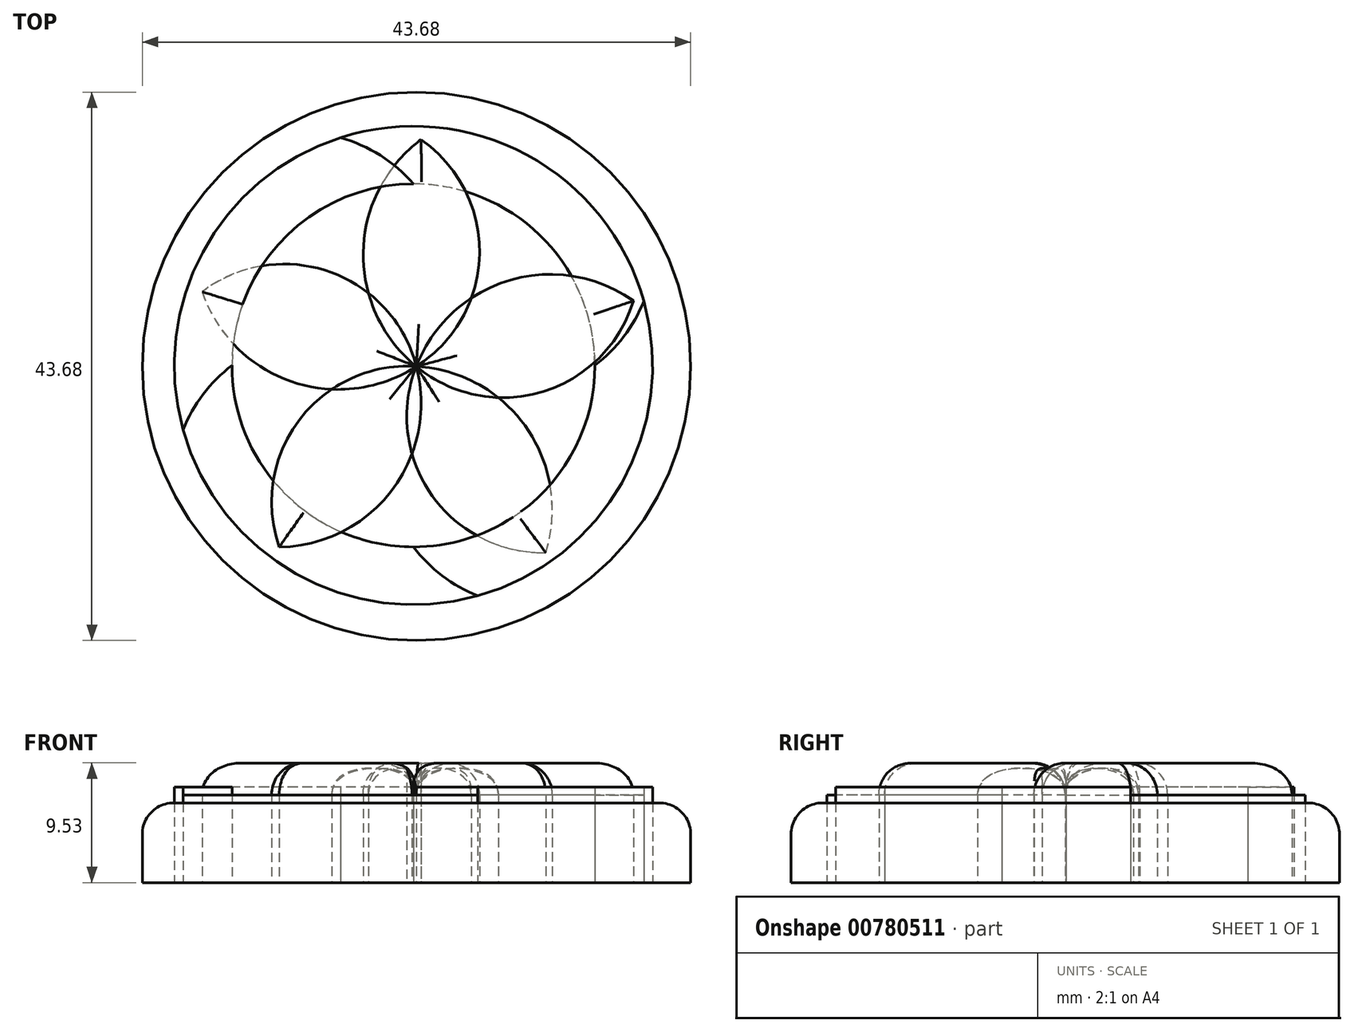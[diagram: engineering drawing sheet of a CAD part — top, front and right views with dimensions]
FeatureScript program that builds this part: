
annotation { "Feature Type Name" : "Feature", "Feature Type Description" : "" }
export const myFeature = defineFeature(function(context is Context, id is Id, definition is map)
    precondition{}
    {
        {
            var Q0;
            Q0=qCreatedBy(makeId("Top.planeOp"),FACE);
            var sketch = newSketch(context, id + "F0", { "sketchPlane" : qUnion([Q0])});
            skCircle(sketch, "E0", {"center": v(0, 0) * mm, "radius": 28.91 * mm});
            skCircle(sketch, "E1", {"center": v(0, 0) * mm, "radius": 38.1 * mm});
            skArc(sketch, "E2", {"start": v(0, 28.91) * mm, "mid": v(-32.59, 32.3) * mm, "end": v(-38.1, 0) * mm});
            skArc(sketch, "E3", {"start": v(-28.91, 0) * mm, "mid": v(-33.5, -33.5) * mm, "end": v(0, -38.1) * mm});
            skArc(sketch, "E4", {"start": v(0, -28.91) * mm, "mid": v(33.5, -33.5) * mm, "end": v(38.1, 0) * mm});
            skArc(sketch, "E5", {"start": v(28.91, 0) * mm, "mid": v(33.5, 33.5) * mm, "end": v(0, 38.1) * mm});
            skArc(sketch, "E6", {"start": v(-14.46, -19.05) * mm, "mid": v(-2.57, -13.06) * mm, "end": v(0, 0) * mm});
            skArc(sketch, "E7", {"start": v(0, 0) * mm, "mid": v(-12.34, -5.65) * mm, "end": v(-14.46, -19.05) * mm});
            skArc(sketch, "E8.1.0", {"start": v(13.76, -20.22) * mm, "mid": v(11.73, -7.06) * mm, "end": v(0.1, -0.58) * mm});
            skArc(sketch, "E8.1.1", {"start": v(0.1, -0.58) * mm, "mid": v(1.66, -14.06) * mm, "end": v(13.76, -20.22) * mm});
            skArc(sketch, "E8.2.0", {"start": v(23.59, 6.25) * mm, "mid": v(10.45, 8.4) * mm, "end": v(0.7, -0.66) * mm});
            skArc(sketch, "E8.2.1", {"start": v(0.7, -0.66) * mm, "mid": v(14, -3.35) * mm, "end": v(23.59, 6.25) * mm});
            skArc(sketch, "E8.3.0", {"start": v(1.45, 23.78) * mm, "mid": v(-4.64, 11.95) * mm, "end": v(0.95, -0.13) * mm});
            skArc(sketch, "E8.3.1", {"start": v(0.95, -0.13) * mm, "mid": v(7.61, 11.7) * mm, "end": v(1.45, 23.78) * mm});
            skArc(sketch, "E8.4.0", {"start": v(-22.06, 8.14) * mm, "mid": v(-12.7, -1.3) * mm, "end": v(0.52, 0.28) * mm});
            skArc(sketch, "E8.4.1", {"start": v(0.52, 0.28) * mm, "mid": v(-8.66, 10.27) * mm, "end": v(-22.06, 8.14) * mm});
            skPoint(sketch, "E8.center", {"position": v(0.45, -0.22) * mm});
            skSolve(sketch);
        }
        {
            var Q0;
            Q0=qCreatedBy(makeId("Top.planeOp"),FACE);
            var sketch = newSketch(context, id + "F1", { "sketchPlane" : qUnion([Q0])});
            skArc(sketch, "E9", {"start": v(-21.38, -28.93) * mm, "mid": v(-3.43, -19.88) * mm, "end": v(0.46, -0.15) * mm});
            skArc(sketch, "E10", {"start": v(0.46, -0.15) * mm, "mid": v(-18.19, -8.68) * mm, "end": v(-21.38, -28.93) * mm});
            skArc(sketch, "E11.1.0", {"start": v(21.08, -29.82) * mm, "mid": v(18.02, -9.94) * mm, "end": v(0.46, -0.15) * mm});
            skArc(sketch, "E11.1.1", {"start": v(0.46, -0.15) * mm, "mid": v(2.8, -20.52) * mm, "end": v(21.08, -29.82) * mm});
            skArc(sketch, "E11.2.0", {"start": v(35.04, 10.3) * mm, "mid": v(15.2, 13.52) * mm, "end": v(0.46, -0.15) * mm});
            skArc(sketch, "E11.2.1", {"start": v(0.46, -0.15) * mm, "mid": v(20.56, -4.21) * mm, "end": v(35.04, 10.3) * mm});
            skArc(sketch, "E11.3.0", {"start": v(1.2, 35.97) * mm, "mid": v(-8, 18.1) * mm, "end": v(0.46, -0.15) * mm});
            skArc(sketch, "E11.3.1", {"start": v(0.46, -0.15) * mm, "mid": v(10.53, 17.7) * mm, "end": v(1.2, 35.97) * mm});
            skArc(sketch, "E11.4.0", {"start": v(-33.66, 11.72) * mm, "mid": v(-19.5, -2.55) * mm, "end": v(0.46, -0.15) * mm});
            skArc(sketch, "E11.4.1", {"start": v(0.46, -0.15) * mm, "mid": v(-13.42, 14.94) * mm, "end": v(-33.66, 11.72) * mm});
            skSolve(sketch);
        }
        {
            var Q0;
            {var subQ1=sQuery(id+"F1.wireOp",EDGE,"E11.3.1");var subQ2=sQuery(id+"F1.wireOp",EDGE,"E11.3.0");var subQ6=makeQuery(id+"F1.imprint","INTERSECT",VERTEX,{"derivedFrom":[subQ2,subQ1]});Q0=makeQuery(id+"F1.imprint","IMPRINT",FACE,{"disambiguationData":[TD([[makeQuery(id+"F1.imprint","IMPRINT",EDGE,{"disambiguationData":[TD([[subQ6,-1.0]])],"derivedFrom":subQ2}),1.0]])]});}
            var Q1;
            {var subQ1=sQuery(id+"F1.wireOp",EDGE,"E11.2.1");var subQ2=sQuery(id+"F1.wireOp",EDGE,"E11.2.0");var subQ6=makeQuery(id+"F1.imprint","INTERSECT",VERTEX,{"derivedFrom":[subQ2,subQ1]});Q1=makeQuery(id+"F1.imprint","IMPRINT",FACE,{"disambiguationData":[TD([[makeQuery(id+"F1.imprint","IMPRINT",EDGE,{"disambiguationData":[TD([[subQ6,-1.0]])],"derivedFrom":subQ2}),1.0]])]});}
            var Q2;
            {var subQ1=sQuery(id+"F1.wireOp",EDGE,"E11.1.1");var subQ2=sQuery(id+"F1.wireOp",EDGE,"E11.1.0");var subQ6=makeQuery(id+"F1.imprint","INTERSECT",VERTEX,{"derivedFrom":[subQ2,subQ1]});Q2=makeQuery(id+"F1.imprint","IMPRINT",FACE,{"disambiguationData":[TD([[makeQuery(id+"F1.imprint","IMPRINT",EDGE,{"disambiguationData":[TD([[subQ6,-1.0]])],"derivedFrom":subQ2}),1.0]])]});}
            var Q3;
            {var subQ0=sQuery(id+"F1.wireOp",EDGE,"E11.4.1");var subQ1=sQuery(id+"F1.wireOp",EDGE,"E11.4.0");var subQ7=makeQuery(id+"F1.imprint","INTERSECT",VERTEX,{"derivedFrom":[subQ1,subQ0]});Q3=makeQuery(id+"F1.imprint","IMPRINT",FACE,{"disambiguationData":[TD([[makeQuery(id+"F1.imprint","IMPRINT",EDGE,{"disambiguationData":[TD([[subQ7,-1.0]])],"derivedFrom":subQ1}),1.0]])]});}
            var Q4;
            {var subQ0=sQuery(id+"F1.wireOp",EDGE,"E10");var subQ1=sQuery(id+"F1.wireOp",EDGE,"E9");var subQ2=makeQuery(id+"F1.imprint","INTERSECT",VERTEX,{"derivedFrom":[subQ1,subQ0]});Q4=makeQuery(id+"F1.imprint","IMPRINT",FACE,{"disambiguationData":[TD([[makeQuery(id+"F1.imprint","IMPRINT",EDGE,{"disambiguationData":[TD([[subQ2,-1.0]])],"derivedFrom":subQ1}),1.0]])]});}
            var Q5;
            Q5=sQuery(id+"F1.wireOp",EDGE,"E11.3.1");
            extrude(context, id + "F2", {"entities" : qUnion([Q0, Q1, Q2, Q3, Q4]), "surfaceEntities" : qUnion([Q5]), "depth" : 19.05 * mm, "offsetDistance" : 25.4 * mm});
        }
        {
            var Q0;
            Q0=qCreatedBy(makeId("Top.planeOp"),FACE);
            var sketch = newSketch(context, id + "F3", { "sketchPlane" : qUnion([Q0])});
            skCircle(sketch, "E12", {"center": v(0.49, -0.14) * mm, "radius": 43.68 * mm});
            skSolve(sketch);
        }
        {
            var Q0;
            Q0=makeQuery(id+"F3.imprint","IMPRINT",FACE,{"disambiguationData":[TD([[makeQuery(id+"F3.imprint","IMPRINT",EDGE,{"derivedFrom":sQuery(id+"F3.wireOp",EDGE,"E12")}),1.0]])]});
            extrude(context, id + "F4", {"entities" : qUnion([Q0]), "depth" : 12.7 * mm, "offsetDistance" : 25.4 * mm});
        }
        {
            var Q0;
            {var subQ0=sQuery(id+"F0.wireOp",EDGE,"E2");var subQ1=sQuery(id+"F0.wireOp",EDGE,"E0");var subQ2=makeQuery(id+"F0.imprint","INTERSECT",VERTEX,{"derivedFrom":[subQ1,subQ0]});Q0=makeQuery(id+"F0.imprint","IMPRINT",FACE,{"disambiguationData":[TD([[makeQuery(id+"F0.imprint","IMPRINT",EDGE,{"disambiguationData":[TD([[subQ2,1.0]])],"derivedFrom":subQ1}),-1.0]])]});}
            var Q1;
            {var subQ0=sQuery(id+"F0.wireOp",EDGE,"E3");var subQ5=sQuery(id+"F0.wireOp",EDGE,"E0");var subQ6=makeQuery(id+"F0.imprint","INTERSECT",VERTEX,{"derivedFrom":[subQ5,subQ0]});Q1=makeQuery(id+"F0.imprint","IMPRINT",FACE,{"disambiguationData":[TD([[makeQuery(id+"F0.imprint","IMPRINT",EDGE,{"disambiguationData":[TD([[subQ6,-1.0]])],"derivedFrom":subQ5}),-1.0]])]});}
            extrude(context, id + "F5", {"entities" : qUnion([Q0, Q1]), "depth" : 13.97 * mm, "offsetDistance" : 25.4 * mm});
        }
        {
            var Q0;
            {var subQ0=sQuery(id+"F0.wireOp",EDGE,"E2");var subQ5=sQuery(id+"F0.wireOp",EDGE,"E0");var subQ6=makeQuery(id+"F0.imprint","INTERSECT",VERTEX,{"derivedFrom":[subQ5,subQ0]});Q0=makeQuery(id+"F0.imprint","IMPRINT",FACE,{"disambiguationData":[TD([[makeQuery(id+"F0.imprint","IMPRINT",EDGE,{"disambiguationData":[TD([[subQ6,-1.0]])],"derivedFrom":subQ5}),-1.0]])]});}
            var Q1;
            {var subQ0=sQuery(id+"F0.wireOp",EDGE,"E4");var subQ1=sQuery(id+"F0.wireOp",EDGE,"E0");var subQ2=makeQuery(id+"F0.imprint","INTERSECT",VERTEX,{"derivedFrom":[subQ1,subQ0]});Q1=makeQuery(id+"F0.imprint","IMPRINT",FACE,{"disambiguationData":[TD([[makeQuery(id+"F0.imprint","IMPRINT",EDGE,{"disambiguationData":[TD([[subQ2,-1.0]])],"derivedFrom":subQ1}),-1.0]])]});}
            extrude(context, id + "F6", {"entities" : qUnion([Q0, Q1]), "depth" : 15.24 * mm, "offsetDistance" : 25.4 * mm});
        }
        {
            var Q0;
            {var subQ0=sQuery(id+"F1.wireOp",EDGE,"E11.4.1");Q0=makeQuery(id+"F2.opExtrude","CAP_EDGE",EDGE,{"disambiguationData":[OSD([subQ0]),TDD([makeQuery(id+"F1.imprint","IMPRINT",EDGE,{"disambiguationData":[TD([[makeQuery(id+"F1.imprint","INTERSECT",VERTEX,{"derivedFrom":[sQuery(id+"F1.wireOp",EDGE,"E11.4.0"),subQ0]}),1.0]])],"derivedFrom":subQ0})])],"isStart":false});}
            var Q1;
            {var subQ0=sQuery(id+"F1.wireOp",EDGE,"E11.4.0");Q1=makeQuery(id+"F2.opExtrude","CAP_EDGE",EDGE,{"disambiguationData":[OSD([subQ0]),TDD([makeQuery(id+"F1.imprint","IMPRINT",EDGE,{"disambiguationData":[TD([[makeQuery(id+"F1.imprint","INTERSECT",VERTEX,{"derivedFrom":[subQ0,sQuery(id+"F1.wireOp",EDGE,"E11.4.1")]}),-1.0]])],"derivedFrom":subQ0})])],"isStart":false});}
            var Q2;
            {var subQ0=sQuery(id+"F1.wireOp",EDGE,"E10");Q2=makeQuery(id+"F2.opExtrude","CAP_EDGE",EDGE,{"disambiguationData":[OSD([subQ0]),TDD([makeQuery(id+"F1.imprint","IMPRINT",EDGE,{"disambiguationData":[TD([[makeQuery(id+"F1.imprint","INTERSECT",VERTEX,{"derivedFrom":[sQuery(id+"F1.wireOp",EDGE,"E9"),subQ0]}),1.0]])],"derivedFrom":subQ0})])],"isStart":false});}
            var Q3;
            {var subQ0=sQuery(id+"F1.wireOp",EDGE,"E11.1.1");Q3=makeQuery(id+"F2.opExtrude","CAP_EDGE",EDGE,{"disambiguationData":[OSD([subQ0]),TDD([makeQuery(id+"F1.imprint","IMPRINT",EDGE,{"disambiguationData":[TD([[makeQuery(id+"F1.imprint","INTERSECT",VERTEX,{"derivedFrom":[sQuery(id+"F1.wireOp",EDGE,"E11.1.0"),subQ0]}),1.0]])],"derivedFrom":subQ0})])],"isStart":false});}
            var Q4;
            {var subQ0=sQuery(id+"F1.wireOp",EDGE,"E11.1.0");Q4=makeQuery(id+"F2.opExtrude","CAP_EDGE",EDGE,{"disambiguationData":[OSD([subQ0]),TDD([makeQuery(id+"F1.imprint","IMPRINT",EDGE,{"disambiguationData":[TD([[makeQuery(id+"F1.imprint","INTERSECT",VERTEX,{"derivedFrom":[subQ0,sQuery(id+"F1.wireOp",EDGE,"E11.1.1")]}),-1.0]])],"derivedFrom":subQ0})])],"isStart":false});}
            var Q5;
            {var subQ0=sQuery(id+"F1.wireOp",EDGE,"E11.2.1");Q5=makeQuery(id+"F2.opExtrude","CAP_EDGE",EDGE,{"disambiguationData":[OSD([subQ0]),TDD([makeQuery(id+"F1.imprint","IMPRINT",EDGE,{"disambiguationData":[TD([[makeQuery(id+"F1.imprint","INTERSECT",VERTEX,{"derivedFrom":[sQuery(id+"F1.wireOp",EDGE,"E11.2.0"),subQ0]}),1.0]])],"derivedFrom":subQ0})])],"isStart":false});}
            var Q6;
            {var subQ0=sQuery(id+"F1.wireOp",EDGE,"E11.3.1");Q6=makeQuery(id+"F2.opExtrude","CAP_EDGE",EDGE,{"disambiguationData":[OSD([subQ0]),TDD([makeQuery(id+"F1.imprint","IMPRINT",EDGE,{"disambiguationData":[TD([[makeQuery(id+"F1.imprint","INTERSECT",VERTEX,{"derivedFrom":[sQuery(id+"F1.wireOp",EDGE,"E11.3.0"),subQ0]}),1.0]])],"derivedFrom":subQ0})])],"isStart":false});}
            var Q7;
            {var subQ0=sQuery(id+"F1.wireOp",EDGE,"E11.3.0");Q7=makeQuery(id+"F2.opExtrude","CAP_EDGE",EDGE,{"disambiguationData":[OSD([subQ0]),TDD([makeQuery(id+"F1.imprint","IMPRINT",EDGE,{"disambiguationData":[TD([[makeQuery(id+"F1.imprint","INTERSECT",VERTEX,{"derivedFrom":[subQ0,sQuery(id+"F1.wireOp",EDGE,"E11.3.1")]}),-1.0]])],"derivedFrom":subQ0})])],"isStart":false});}
            var Q8;
            {var subQ0=sQuery(id+"F1.wireOp",EDGE,"E11.2.0");Q8=makeQuery(id+"F2.opExtrude","CAP_EDGE",EDGE,{"disambiguationData":[OSD([subQ0]),TDD([makeQuery(id+"F1.imprint","IMPRINT",EDGE,{"disambiguationData":[TD([[makeQuery(id+"F1.imprint","INTERSECT",VERTEX,{"derivedFrom":[subQ0,sQuery(id+"F1.wireOp",EDGE,"E11.2.1")]}),-1.0]])],"derivedFrom":subQ0})])],"isStart":false});}
            var Q9;
            {var subQ0=sQuery(id+"F1.wireOp",EDGE,"E9");Q9=makeQuery(id+"F2.opExtrude","CAP_EDGE",EDGE,{"disambiguationData":[OSD([subQ0]),TDD([makeQuery(id+"F1.imprint","IMPRINT",EDGE,{"disambiguationData":[TD([[makeQuery(id+"F1.imprint","INTERSECT",VERTEX,{"derivedFrom":[subQ0,sQuery(id+"F1.wireOp",EDGE,"E10")]}),-1.0]])],"derivedFrom":subQ0})])],"isStart":false});}
            fillet(context, id + "F7", {"entities" : qUnion([Q0, Q1, Q2, Q3, Q4, Q5, Q6, Q7, Q8, Q9]), "radius" : 5 * mm, "tangentPropagation" : true, "allowEdgeOverflow" : false});
        }
        {
            var Q0;
            Q0=makeQuery(id+"F4.opExtrude","CAP_EDGE",EDGE,{"disambiguationData":[OSD([sQuery(id+"F3.wireOp",EDGE,"E12")])],"isStart":false});
            fillet(context, id + "F8", {"entities" : qUnion([Q0]), "radius" : 5 * mm, "tangentPropagation" : true, "allowEdgeOverflow" : false});
        }
        {
            var Q0;
            Q0=makeQuery(id+"F2.opExtrude","SWEPT_BODY",BODY,{"disambiguationData":[OSD([sQuery(id+"F1.wireOp",EDGE,"E9"),sQuery(id+"F1.wireOp",EDGE,"E10"),sQuery(id+"F1.wireOp",EDGE,"E11.1.1"),sQuery(id+"F1.wireOp",EDGE,"E11.4.0")])]});
            var Q1;
            Q1=makeQuery(id+"F2.opExtrude","SWEPT_BODY",BODY,{"disambiguationData":[OSD([sQuery(id+"F1.wireOp",EDGE,"E10"),sQuery(id+"F1.wireOp",EDGE,"E11.3.0"),sQuery(id+"F1.wireOp",EDGE,"E11.4.0"),sQuery(id+"F1.wireOp",EDGE,"E11.4.1")])]});
            var Q2;
            Q2=makeQuery(id+"F2.opExtrude","SWEPT_BODY",BODY,{"disambiguationData":[OSD([sQuery(id+"F1.wireOp",EDGE,"E11.2.0"),sQuery(id+"F1.wireOp",EDGE,"E11.3.0"),sQuery(id+"F1.wireOp",EDGE,"E11.3.1"),sQuery(id+"F1.wireOp",EDGE,"E11.4.1")])]});
            var Q3;
            Q3=makeQuery(id+"F2.opExtrude","SWEPT_BODY",BODY,{"disambiguationData":[OSD([sQuery(id+"F1.wireOp",EDGE,"E9"),sQuery(id+"F1.wireOp",EDGE,"E11.1.0"),sQuery(id+"F1.wireOp",EDGE,"E11.1.1"),sQuery(id+"F1.wireOp",EDGE,"E11.2.1")])]});
            var Q4;
            Q4=makeQuery(id+"F2.opExtrude","SWEPT_BODY",BODY,{"disambiguationData":[OSD([sQuery(id+"F1.wireOp",EDGE,"E11.1.0"),sQuery(id+"F1.wireOp",EDGE,"E11.2.0"),sQuery(id+"F1.wireOp",EDGE,"E11.2.1"),sQuery(id+"F1.wireOp",EDGE,"E11.3.1")])]});
            var Q5;
            Q5=makeQuery(id+"F4.opExtrude","SWEPT_BODY",BODY,{"disambiguationData":[OSD([sQuery(id+"F3.wireOp",EDGE,"E12")])]});
            var Q6;
            Q6=makeQuery(id+"F5.opExtrude","SWEPT_BODY",BODY,{"disambiguationData":[OSD([sQuery(id+"F0.wireOp",EDGE,"E0"),sQuery(id+"F0.wireOp",EDGE,"E1"),sQuery(id+"F0.wireOp",EDGE,"E3"),sQuery(id+"F0.wireOp",EDGE,"E4")])]});
            var Q7;
            Q7=makeQuery(id+"F6.opExtrude","SWEPT_BODY",BODY,{"disambiguationData":[OSD([sQuery(id+"F0.wireOp",EDGE,"E0"),sQuery(id+"F0.wireOp",EDGE,"E1"),sQuery(id+"F0.wireOp",EDGE,"E4"),sQuery(id+"F0.wireOp",EDGE,"E5")])]});
            var Q8;
            Q8=makeQuery(id+"F5.opExtrude","SWEPT_BODY",BODY,{"disambiguationData":[OSD([sQuery(id+"F0.wireOp",EDGE,"E0"),sQuery(id+"F0.wireOp",EDGE,"E1"),sQuery(id+"F0.wireOp",EDGE,"E2"),sQuery(id+"F0.wireOp",EDGE,"E5")])]});
            var Q9;
            Q9=makeQuery(id+"F6.opExtrude","SWEPT_BODY",BODY,{"disambiguationData":[OSD([sQuery(id+"F0.wireOp",EDGE,"E0"),sQuery(id+"F0.wireOp",EDGE,"E1"),sQuery(id+"F0.wireOp",EDGE,"E2"),sQuery(id+"F0.wireOp",EDGE,"E3")])]});
            var Q10;
            Q10=qCreatedBy(makeId("Origin.pointOp"),VERTEX);
            transform(context, id + "F9", {"entities" : qUnion([Q0, Q1, Q2, Q3, Q4, Q5, Q6, Q7, Q8, Q9]), "transformType" : TransformType.SCALE_UNIFORMLY, "scale" : 0.5, "scalePoint" : qUnion([Q10]), "makeCopy" : false});
        }
    });
